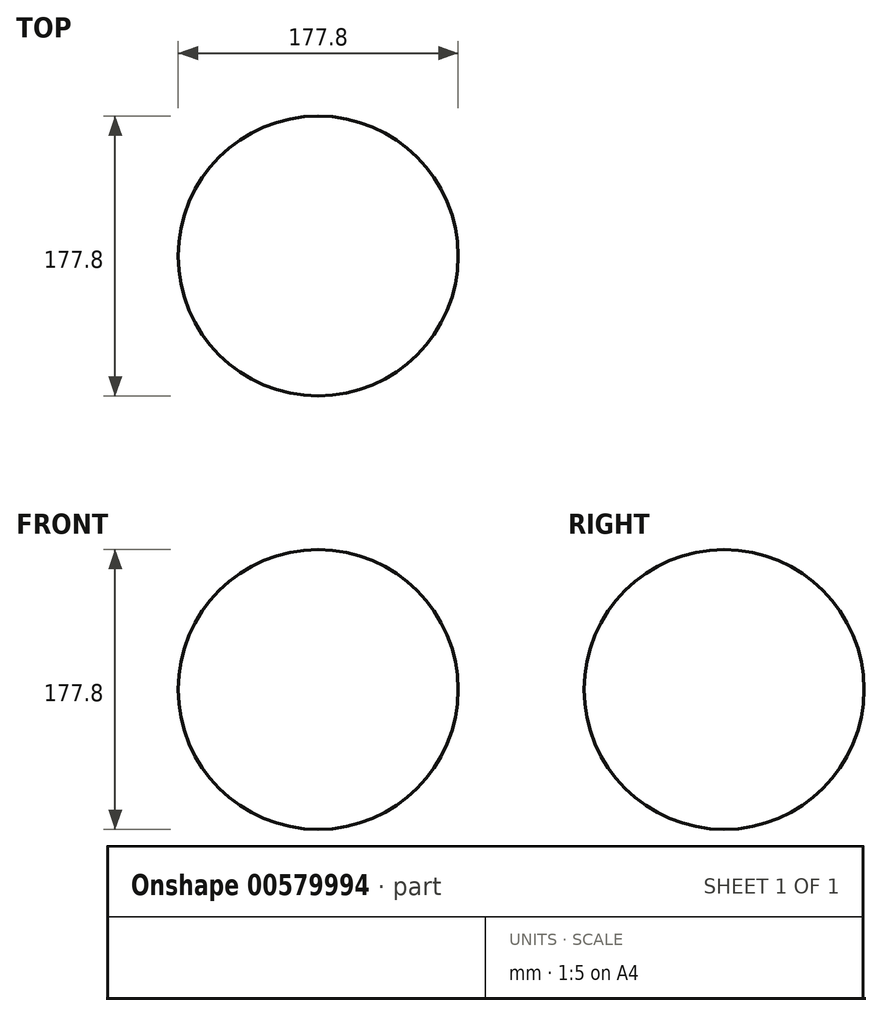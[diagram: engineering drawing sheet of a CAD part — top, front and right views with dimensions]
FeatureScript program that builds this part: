
annotation { "Feature Type Name" : "Feature", "Feature Type Description" : "" }
export const myFeature = defineFeature(function(context is Context, id is Id, definition is map)
    precondition{}
    {
        {
            var Q0;
            Q0=qCreatedBy(makeId("Front.planeOp"),FACE);
            var sketch = newSketch(context, id + "F0", { "sketchPlane" : qUnion([Q0])});
            skLineSegment(sketch, "E0", {"start": v(-89.07, 0) * mm, "end": v(88.73, 0) * mm});
            skArc(sketch, "E1", {"start": v(88.73, 0) * mm, "mid": v(-0.17, 88.9) * mm, "end": v(-89.07, 0) * mm});
            skSolve(sketch);
        }
        {
            var Q0;
            Q0=makeQuery(id+"F0.imprint","IMPRINT",FACE,{"disambiguationData":[TD([[makeQuery(id+"F0.imprint","IMPRINT",EDGE,{"derivedFrom":sQuery(id+"F0.wireOp",EDGE,"E0")}),1.0]])]});
            var Q1;
            Q1=sQuery(id+"F0.wireOp",EDGE,"E0");
            revolve(context, id + "F1", {"entities" : qUnion([Q0]), "axis" : qUnion([Q1]), "revolveType" : RevolveType.FULL});
        }
    });
